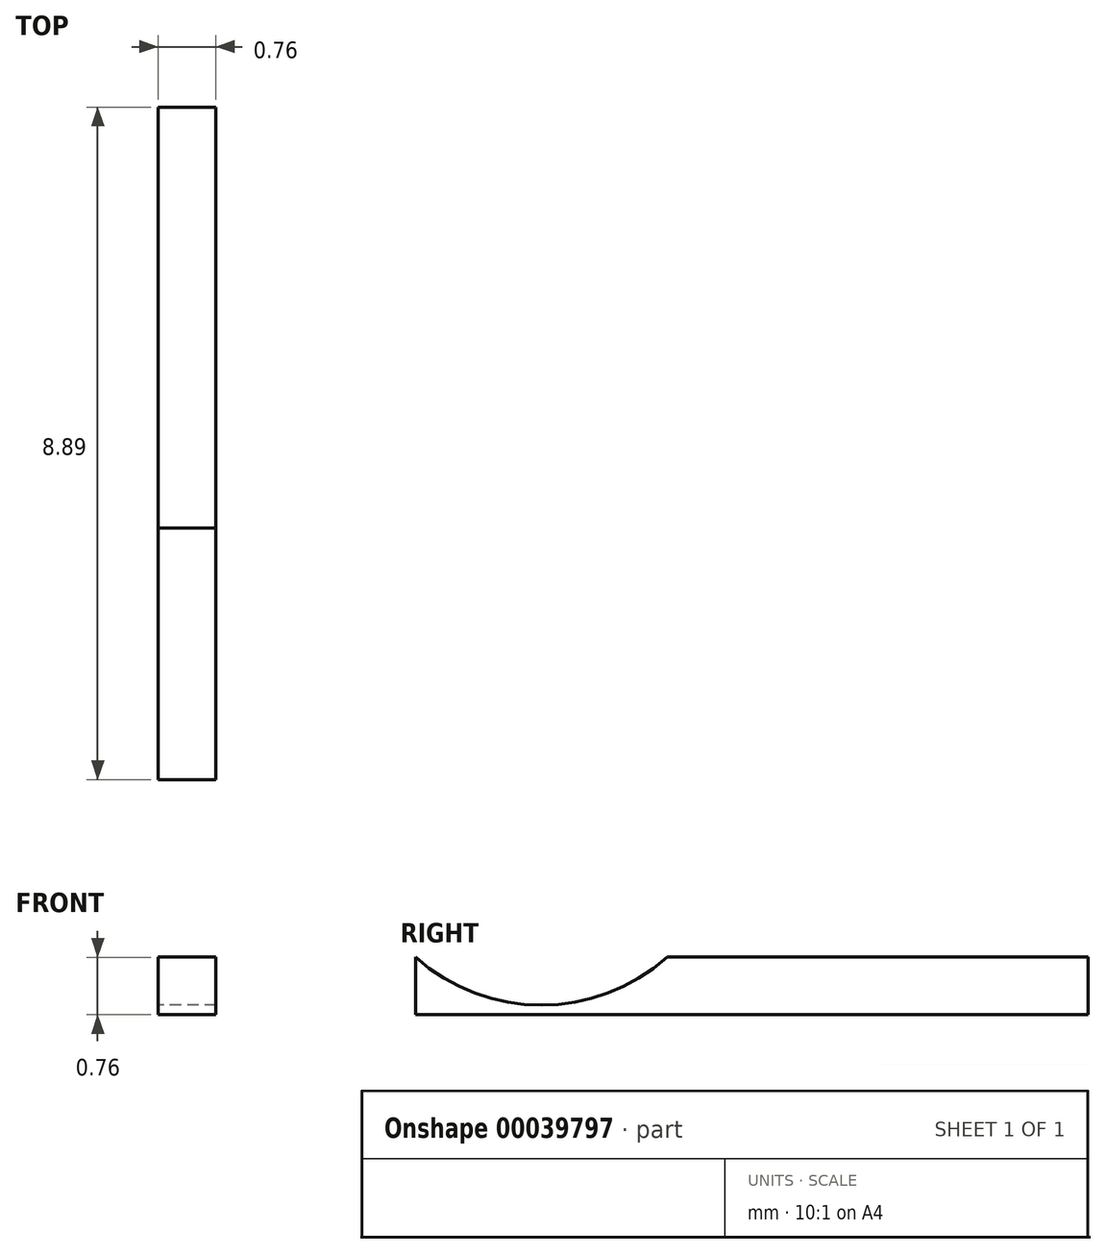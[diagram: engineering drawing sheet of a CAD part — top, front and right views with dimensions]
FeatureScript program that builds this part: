
annotation { "Feature Type Name" : "Feature", "Feature Type Description" : "" }
export const myFeature = defineFeature(function(context is Context, id is Id, definition is map)
    precondition{}
    {
        {
            var Q0;
            Q0=qCreatedBy(makeId("Right.planeOp"),FACE);
            var sketch = newSketch(context, id + "F0", { "sketchPlane" : qUnion([Q0])});
            skLineSegment(sketch, "E0", {"start": v(0, 0) * mm, "end": v(8.9, 0) * mm});
            skLineSegment(sketch, "E1", {"start": v(8.9, 0) * mm, "end": v(8.9, 0.76) * mm});
            skLineSegment(sketch, "E2", {"start": v(0, 0.76) * mm, "end": v(0, 0) * mm});
            skLineSegment(sketch, "E3", {"start": v(7.28, 1.27) * mm, "end": v(7.28, 1.14) * mm});
            skLineSegment(sketch, "E4", {"start": v(7.23, 0.76) * mm, "end": v(7.23, 0.13) * mm});
            skLineSegment(sketch, "E5", {"start": v(5.56, 0.76) * mm, "end": v(8.9, 0.76) * mm});
            skLineSegment(sketch, "E6", {"start": v(1.66, 0.76) * mm, "end": v(1.66, 0.13) * mm});
            skArc(sketch, "E7", {"start": v(0, 0.76) * mm, "mid": v(1.66, 0.13) * mm, "end": v(3.33, 0.76) * mm});
            skLineSegment(sketch, "E8", {"start": v(3.33, 0.76) * mm, "end": v(5.56, 0.76) * mm});
            skSolve(sketch);
        }
        {
            var Q0;
            Q0 = qSketchRegion(id + "F0", true);
            extrude(context, id + "F1", {"entities" : qUnion([Q0]), "depth" : 0.76 * mm});
        }
    });
